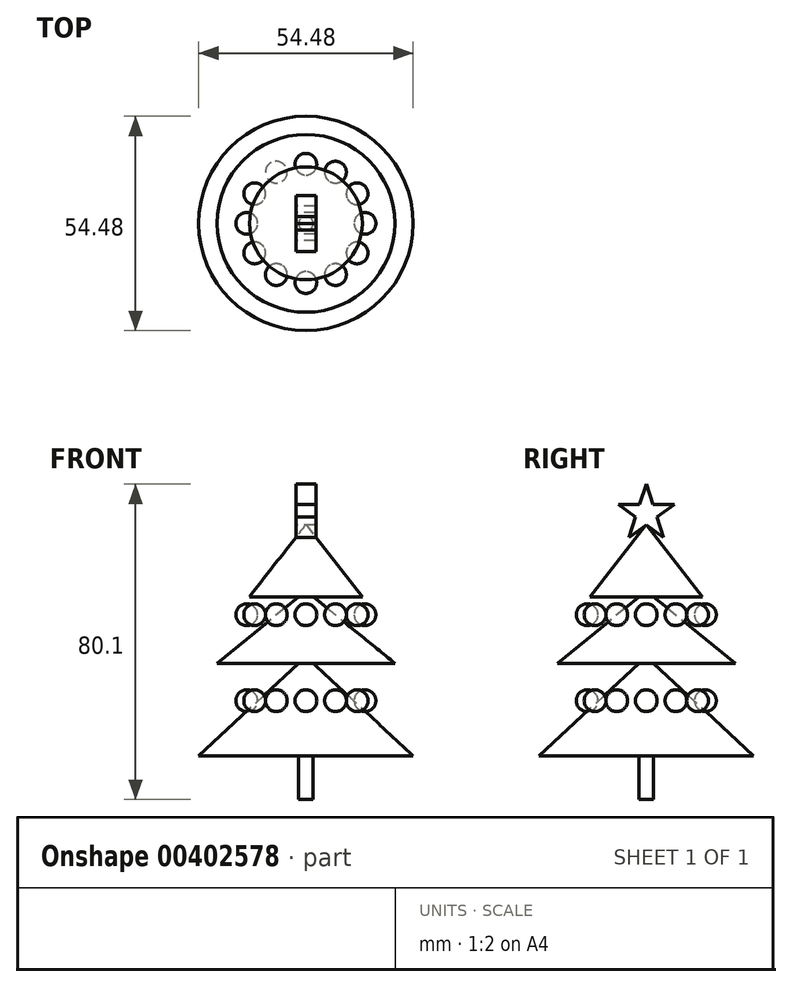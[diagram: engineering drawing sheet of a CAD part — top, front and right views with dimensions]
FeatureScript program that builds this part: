
annotation { "Feature Type Name" : "Feature", "Feature Type Description" : "" }
export const myFeature = defineFeature(function(context is Context, id is Id, definition is map)
    precondition{}
    {
        {
            var Q0;
            Q0=qCreatedBy(makeId("Right.planeOp"),FACE);
            var sketch = newSketch(context, id + "F0", { "sketchPlane" : qUnion([Q0])});
            skLineSegment(sketch, "E0", {"start": v(0, 51.6) * mm, "end": v(0, -18.25) * mm});
            skLineSegment(sketch, "E1", {"start": v(0, 51.6) * mm, "end": v(14.32, 33.23) * mm});
            skLineSegment(sketch, "E2", {"start": v(14.32, 33.23) * mm, "end": v(1.84, 33.23) * mm});
            skLineSegment(sketch, "E3", {"start": v(1.84, 33.23) * mm, "end": v(22.58, 16.34) * mm});
            skLineSegment(sketch, "E4", {"start": v(22.58, 16.34) * mm, "end": v(1.84, 16.34) * mm});
            skLineSegment(sketch, "E5", {"start": v(1.84, 16.34) * mm, "end": v(27.24, -7.16) * mm});
            skLineSegment(sketch, "E6", {"start": v(27.24, -7.16) * mm, "end": v(1.84, -7.16) * mm});
            skLineSegment(sketch, "E7", {"start": v(1.84, -7.16) * mm, "end": v(1.84, -19.46) * mm});
            skLineSegment(sketch, "E8", {"start": v(1.84, -18.25) * mm, "end": v(1.84, -19.46) * mm});
            skLineSegment(sketch, "E9", {"start": v(1.84, -18.25) * mm, "end": v(0, -18.25) * mm});
            skSolve(sketch);
        }
        {
            var Q0;
            Q0=makeQuery(id+"F0.imprint","IMPRINT",FACE,{"disambiguationData":[TD([[makeQuery(id+"F0.imprint","IMPRINT",EDGE,{"derivedFrom":sQuery(id+"F0.wireOp",EDGE,"E0")}),1.0]])]});
            var Q1;
            Q1=sQuery(id+"F0.wireOp",EDGE,"E0");
            revolve(context, id + "F1", {"entities" : qUnion([Q0]), "axis" : qUnion([Q1]), "revolveType" : RevolveType.FULL});
        }
        {
            var Q0;
            Q0=qCreatedBy(makeId("Right.planeOp"),FACE);
            var sketch = newSketch(context, id + "F2", { "sketchPlane" : qUnion([Q0])});
            skCircle(sketch, "E10.cCircle", {"center": v(0, 54.36) * mm, "radius": 7.48 * mm, "construction": true});
            skLineSegment(sketch, "E10.0", {"start": v(-4.4, 48.3) * mm, "end": v(-7.12, 56.67) * mm, "construction": true});
            skLineSegment(sketch, "E10.1", {"start": v(-7.12, 56.67) * mm, "end": v(0, 61.85) * mm, "construction": true});
            skLineSegment(sketch, "E10.2", {"start": v(0, 61.85) * mm, "end": v(7.12, 56.67) * mm, "construction": true});
            skLineSegment(sketch, "E10.3", {"start": v(7.12, 56.67) * mm, "end": v(4.4, 48.3) * mm, "construction": true});
            skLineSegment(sketch, "E10.4", {"start": v(4.4, 48.3) * mm, "end": v(-4.4, 48.3) * mm, "construction": true});
            skLineSegment(sketch, "E11", {"start": v(4.4, 48.3) * mm, "end": v(2.72, 53.48) * mm});
            skLineSegment(sketch, "E12", {"start": v(0, 61.85) * mm, "end": v(-1.68, 56.67) * mm});
            skLineSegment(sketch, "E13", {"start": v(-4.4, 48.3) * mm, "end": v(0, 51.5) * mm});
            skLineSegment(sketch, "E14", {"start": v(7.12, 56.67) * mm, "end": v(1.68, 56.67) * mm});
            skLineSegment(sketch, "E15", {"start": v(-7.12, 56.67) * mm, "end": v(-2.72, 53.48) * mm});
            skLineSegment(sketch, "E16.trimOffspring", {"start": v(-1.68, 56.67) * mm, "end": v(-7.12, 56.67) * mm});
            skLineSegment(sketch, "E17.trimOffspring", {"start": v(1.68, 56.67) * mm, "end": v(0, 61.85) * mm});
            skLineSegment(sketch, "E18.trimOffspring", {"start": v(2.72, 53.48) * mm, "end": v(7.12, 56.67) * mm});
            skLineSegment(sketch, "E19.trimOffspring", {"start": v(0, 51.5) * mm, "end": v(4.4, 48.3) * mm});
            skLineSegment(sketch, "E20.trimOffspring", {"start": v(-2.72, 53.48) * mm, "end": v(-4.4, 48.3) * mm});
            skSolve(sketch);
        }
        {
            var Q0;
            Q0=makeQuery(id+"F2.imprint","IMPRINT",FACE,{"disambiguationData":[TD([[makeQuery(id+"F2.imprint","IMPRINT",EDGE,{"derivedFrom":sQuery(id+"F2.wireOp",EDGE,"E11")}),1.0]])]});
            extrude(context, id + "F3", {"entities" : qUnion([Q0]), "endBound" : BoundingType.SYMMETRIC, "depth" : 5.08 * mm});
        }
        {
            var Q0;
            Q0=makeQuery(id+"F1.opRevolve","SWEPT_FACE",FACE,{"disambiguationData":[OSD([sQuery(id+"F0.wireOp",EDGE,"E2")])]});
            var sketch = newSketch(context, id + "F4", { "sketchPlane" : qUnion([Q0])});
            skLineSegment(sketch, "E21", {"start": v(0, -28.2) * mm, "end": v(0, -22.68) * mm});
            skArc(sketch, "E22", {"start": v(0, -28.2) * mm, "mid": v(2.77, -25.44) * mm, "end": v(0, -22.68) * mm});
            skSolve(sketch);
        }
        {
            var Q0;
            Q0=makeQuery(id+"F4.imprint","IMPRINT",FACE,{"disambiguationData":[TD([[makeQuery(id+"F4.imprint","IMPRINT",EDGE,{"derivedFrom":sQuery(id+"F4.wireOp",EDGE,"E21")}),-1.0]])]});
            var Q1;
            Q1=sQuery(id+"F4.wireOp",EDGE,"E21");
            revolve(context, id + "F5", {"entities" : qUnion([Q0]), "axis" : qUnion([Q1]), "revolveType" : RevolveType.FULL});
        }
        {
            var Q0;
            Q0=makeQuery(id+"F5.opRevolve","SWEPT_BODY",BODY,{"disambiguationData":[OSD([sQuery(id+"F4.wireOp",EDGE,"E21"),sQuery(id+"F4.wireOp",EDGE,"E22")])]});
            transform(context, id + "F6", {"entities" : qUnion([Q0]), "transformType" : TransformType.TRANSLATION_3D, "dx" : 0 * mm, "dy" : -10.4 * mm, "dz" : -26.42 * mm, "makeCopy" : false});
        }
        {
            var Q0;
            Q0=makeQuery(id+"F5.opRevolve","SWEPT_BODY",BODY,{"disambiguationData":[OSD([sQuery(id+"F4.wireOp",EDGE,"E21"),sQuery(id+"F4.wireOp",EDGE,"E22")])]});
            var Q1;
            Q1=makeQuery(id+"F1.opRevolve","SWEPT_FACE",FACE,{"disambiguationData":[OSD([sQuery(id+"F0.wireOp",EDGE,"E7")])]});
            circularPattern(context, id + "F7", {"entities" : qUnion([Q0]), "axis" : qUnion([Q1]), "angle" : 360 * degree, "instanceCount" : 12, "equalSpace" : true});
        }
        {
            var Q0;
            Q0=makeQuery(id+"F5.opRevolve","SWEPT_BODY",BODY,{"disambiguationData":[OSD([sQuery(id+"F4.wireOp",EDGE,"E21"),sQuery(id+"F4.wireOp",EDGE,"E22")])]});
            var Q1;
            Q1=makeQuery(id+"F7.opPattern","COPY",BODY,{"derivedFrom":makeQuery(id+"F5.opRevolve","SWEPT_BODY",BODY,{"disambiguationData":[OSD([sQuery(id+"F4.wireOp",EDGE,"E21"),sQuery(id+"F4.wireOp",EDGE,"E22")])]}),"instanceName":"11"});
            var Q2;
            Q2=makeQuery(id+"F7.opPattern","COPY",BODY,{"derivedFrom":makeQuery(id+"F5.opRevolve","SWEPT_BODY",BODY,{"disambiguationData":[OSD([sQuery(id+"F4.wireOp",EDGE,"E21"),sQuery(id+"F4.wireOp",EDGE,"E22")])]}),"instanceName":"10"});
            var Q3;
            Q3=makeQuery(id+"F7.opPattern","COPY",BODY,{"derivedFrom":makeQuery(id+"F5.opRevolve","SWEPT_BODY",BODY,{"disambiguationData":[OSD([sQuery(id+"F4.wireOp",EDGE,"E21"),sQuery(id+"F4.wireOp",EDGE,"E22")])]}),"instanceName":"9"});
            var Q4;
            Q4=makeQuery(id+"F7.opPattern","COPY",BODY,{"derivedFrom":makeQuery(id+"F5.opRevolve","SWEPT_BODY",BODY,{"disambiguationData":[OSD([sQuery(id+"F4.wireOp",EDGE,"E21"),sQuery(id+"F4.wireOp",EDGE,"E22")])]}),"instanceName":"8"});
            var Q5;
            Q5=makeQuery(id+"F7.opPattern","COPY",BODY,{"derivedFrom":makeQuery(id+"F5.opRevolve","SWEPT_BODY",BODY,{"disambiguationData":[OSD([sQuery(id+"F4.wireOp",EDGE,"E21"),sQuery(id+"F4.wireOp",EDGE,"E22")])]}),"instanceName":"7"});
            var Q6;
            Q6=makeQuery(id+"F7.opPattern","COPY",BODY,{"derivedFrom":makeQuery(id+"F5.opRevolve","SWEPT_BODY",BODY,{"disambiguationData":[OSD([sQuery(id+"F4.wireOp",EDGE,"E21"),sQuery(id+"F4.wireOp",EDGE,"E22")])]}),"instanceName":"6"});
            var Q7;
            Q7=makeQuery(id+"F7.opPattern","COPY",BODY,{"derivedFrom":makeQuery(id+"F5.opRevolve","SWEPT_BODY",BODY,{"disambiguationData":[OSD([sQuery(id+"F4.wireOp",EDGE,"E21"),sQuery(id+"F4.wireOp",EDGE,"E22")])]}),"instanceName":"5"});
            var Q8;
            Q8=makeQuery(id+"F7.opPattern","COPY",BODY,{"derivedFrom":makeQuery(id+"F5.opRevolve","SWEPT_BODY",BODY,{"disambiguationData":[OSD([sQuery(id+"F4.wireOp",EDGE,"E21"),sQuery(id+"F4.wireOp",EDGE,"E22")])]}),"instanceName":"4"});
            var Q9;
            Q9=makeQuery(id+"F7.opPattern","COPY",BODY,{"derivedFrom":makeQuery(id+"F5.opRevolve","SWEPT_BODY",BODY,{"disambiguationData":[OSD([sQuery(id+"F4.wireOp",EDGE,"E21"),sQuery(id+"F4.wireOp",EDGE,"E22")])]}),"instanceName":"2"});
            var Q10;
            Q10=makeQuery(id+"F7.opPattern","COPY",BODY,{"derivedFrom":makeQuery(id+"F5.opRevolve","SWEPT_BODY",BODY,{"disambiguationData":[OSD([sQuery(id+"F4.wireOp",EDGE,"E21"),sQuery(id+"F4.wireOp",EDGE,"E22")])]}),"instanceName":"3"});
            transform(context, id + "F8", {"entities" : qUnion([Q0, Q1, Q2, Q3, Q4, Q5, Q6, Q7, Q8, Q9, Q10]), "transformType" : TransformType.TRANSLATION_3D, "dx" : 0 * mm, "dy" : 0 * mm, "dz" : 21.84 * mm, "makeCopy" : true});
        }
    });
